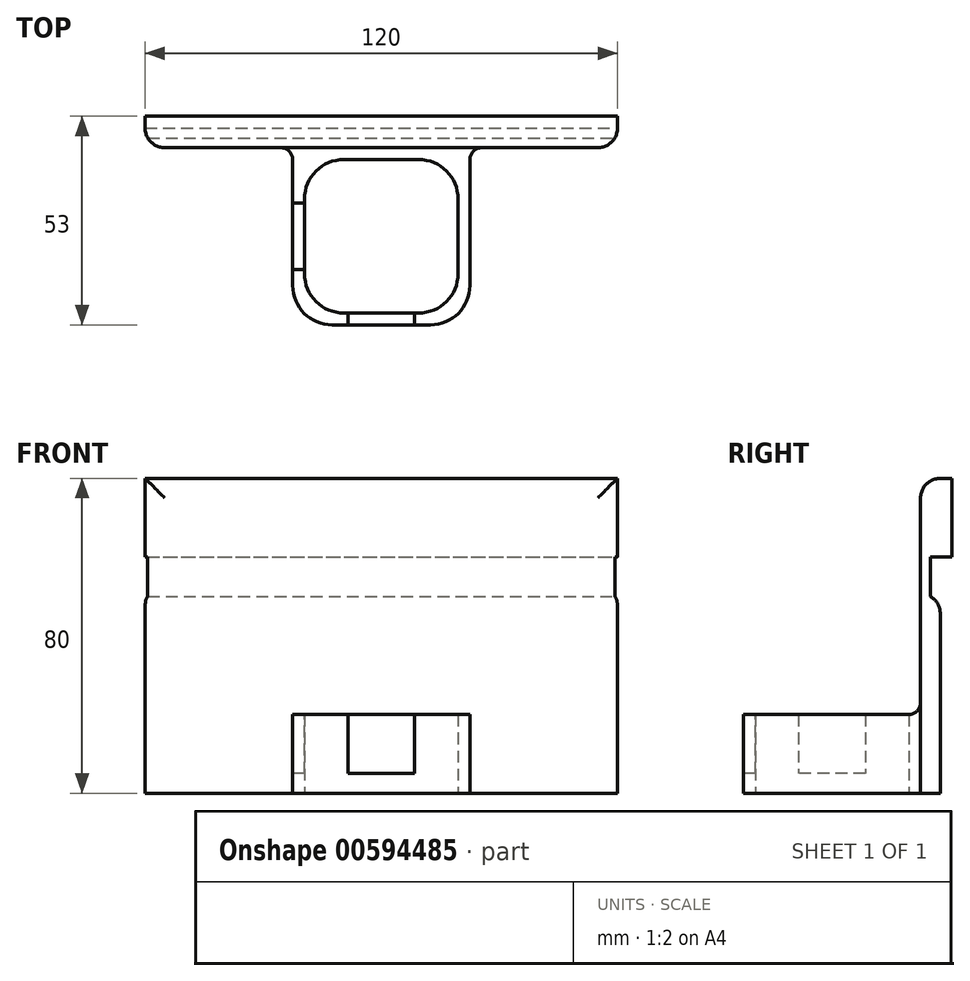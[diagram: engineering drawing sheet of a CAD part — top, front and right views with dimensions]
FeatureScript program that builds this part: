
annotation { "Feature Type Name" : "Feature", "Feature Type Description" : "" }
export const myFeature = defineFeature(function(context is Context, id is Id, definition is map)
    precondition{}
    {
        {
            var Q0;
            Q0=qCreatedBy(makeId("Top.planeOp"),FACE);
            var sketch = newSketch(context, id + "F0", { "sketchPlane" : qUnion([Q0])});
            skLineSegment(sketch, "E0.bottom", {"start": v(-23.05, 24.16) * mm, "end": v(-4.05, 24.16) * mm});
            skLineSegment(sketch, "E0.top", {"start": v(-23.05, -14.84) * mm, "end": v(-4.05, -14.84) * mm});
            skLineSegment(sketch, "E0.left", {"start": v(-33.05, 14.16) * mm, "end": v(-33.05, -4.84) * mm});
            skLineSegment(sketch, "E0.right", {"start": v(5.95, 14.16) * mm, "end": v(5.95, -4.84) * mm});
            skPoint(sketch, "E1.visualSharp", {"position": v(-33.05, 24.16) * mm});
            skArc(sketch, "E1.filletArc", {"start": v(-23.05, 24.16) * mm, "mid": v(-30.12, 21.23) * mm, "end": v(-33.05, 14.16) * mm});
            skPoint(sketch, "E2.visualSharp", {"position": v(5.95, 24.16) * mm});
            skArc(sketch, "E2.filletArc", {"start": v(5.95, 14.16) * mm, "mid": v(3.02, 21.23) * mm, "end": v(-4.05, 24.16) * mm});
            skPoint(sketch, "E3.visualSharp", {"position": v(-33.05, -14.84) * mm});
            skArc(sketch, "E3.filletArc", {"start": v(-33.05, -4.84) * mm, "mid": v(-30.12, -11.9) * mm, "end": v(-23.05, -14.84) * mm});
            skPoint(sketch, "E4.visualSharp", {"position": v(5.95, -14.84) * mm});
            skArc(sketch, "E4.filletArc", {"start": v(-4.05, -14.84) * mm, "mid": v(3.02, -11.9) * mm, "end": v(5.95, -4.84) * mm});
            skLineSegment(sketch, "E5.bottom", {"start": v(-36.05, 27.16) * mm, "end": v(8.95, 27.16) * mm});
            skLineSegment(sketch, "E5.top", {"start": v(-26.05, -17.84) * mm, "end": v(-1.05, -17.84) * mm});
            skLineSegment(sketch, "E5.left", {"start": v(-36.05, 27.16) * mm, "end": v(-36.05, -7.84) * mm});
            skLineSegment(sketch, "E5.right", {"start": v(8.95, 27.16) * mm, "end": v(8.95, -7.84) * mm});
            skPoint(sketch, "E6.visualSharp", {"position": v(-36.05, -17.84) * mm});
            skArc(sketch, "E6.filletArc", {"start": v(-36.05, -7.84) * mm, "mid": v(-33.12, -14.9) * mm, "end": v(-26.05, -17.84) * mm});
            skPoint(sketch, "E7.visualSharp", {"position": v(8.95, -17.84) * mm});
            skArc(sketch, "E7.filletArc", {"start": v(-1.05, -17.84) * mm, "mid": v(6.02, -14.9) * mm, "end": v(8.95, -7.84) * mm});
            skSolve(sketch);
        }
        {
            var Q0;
            Q0 = qSketchRegion(id + "F0", true);
            extrude(context, id + "F1", {"entities" : qUnion([Q0]), "depth" : 20 * mm, "offsetDistance" : 25 * mm});
        }
        {
            var Q0;
            Q0=makeQuery(id+"F1.opExtrude","SWEPT_FACE",FACE,{"disambiguationData":[OSD([sQuery(id+"F0.wireOp",EDGE,"E5.top")])]});
            var sketch = newSketch(context, id + "F2", { "sketchPlane" : qUnion([Q0])});
            skLineSegment(sketch, "E8.bottom", {"start": v(-22.05, 20) * mm, "end": v(-5.05, 20) * mm});
            skLineSegment(sketch, "E8.top", {"start": v(-22.05, 5) * mm, "end": v(-5.05, 5) * mm});
            skLineSegment(sketch, "E8.left", {"start": v(-22.05, 20) * mm, "end": v(-22.05, 5) * mm});
            skLineSegment(sketch, "E8.right", {"start": v(-5.05, 20) * mm, "end": v(-5.05, 5) * mm});
            skSolve(sketch);
        }
        {
            var Q0;
            Q0 = qSketchRegion(id + "F2", true);
            extrude(context, id + "F3", {"entities" : qUnion([Q0]), "operationType" : NewBodyOperationType.REMOVE, "oppositeDirection" : true, "depth" : 5 * mm, "offsetDistance" : 25 * mm});
        }
        {
            var Q0;
            Q0=makeQuery(id+"F1.opExtrude","SWEPT_FACE",FACE,{"disambiguationData":[OSD([sQuery(id+"F0.wireOp",EDGE,"E5.left")])]});
            var sketch = newSketch(context, id + "F4", { "sketchPlane" : qUnion([Q0])});
            skLineSegment(sketch, "E9.bottom", {"start": v(-13.16, 20) * mm, "end": v(3.84, 20) * mm});
            skLineSegment(sketch, "E9.top", {"start": v(-13.16, 5) * mm, "end": v(3.84, 5) * mm});
            skLineSegment(sketch, "E9.left", {"start": v(-13.16, 20) * mm, "end": v(-13.16, 5) * mm});
            skLineSegment(sketch, "E9.right", {"start": v(3.84, 20) * mm, "end": v(3.84, 5) * mm});
            skSolve(sketch);
        }
        {
            var Q0;
            Q0 = qSketchRegion(id + "F4", true);
            extrude(context, id + "F5", {"entities" : qUnion([Q0]), "operationType" : NewBodyOperationType.REMOVE, "oppositeDirection" : true, "depth" : 5 * mm, "offsetDistance" : 25 * mm});
        }
        {
            var Q0;
            Q0=makeQuery(id+"F1.opExtrude","SWEPT_FACE",FACE,{"disambiguationData":[OSD([sQuery(id+"F0.wireOp",EDGE,"E5.bottom")])]});
            var sketch = newSketch(context, id + "F6", { "sketchPlane" : qUnion([Q0])});
            skLineSegment(sketch, "E10.bottom", {"start": v(73.55, 0) * mm, "end": v(-46.45, 0) * mm});
            skLineSegment(sketch, "E10.top", {"start": v(73.55, 80) * mm, "end": v(-46.45, 80) * mm});
            skLineSegment(sketch, "E10.left", {"start": v(73.55, 0) * mm, "end": v(73.55, 80) * mm});
            skLineSegment(sketch, "E10.right", {"start": v(-46.45, 0) * mm, "end": v(-46.45, 80) * mm});
            skSolve(sketch);
        }
        {
            var Q0;
            Q0 = qSketchRegion(id + "F6", true);
            extrude(context, id + "F7", {"entities" : qUnion([Q0]), "operationType" : NewBodyOperationType.ADD, "depth" : 5 * mm, "offsetDistance" : 25 * mm});
        }
        {
            var Q0;
            Q0=makeQuery(id+"F7.boolean.opBoolean","MERGE",FACE,{"derivedFrom":[makeQuery(id+"F1.opExtrude","CAP_FACE",FACE,{"disambiguationData":[OSD([sQuery(id+"F0.wireOp",EDGE,"E0.bottom"),sQuery(id+"F0.wireOp",EDGE,"E0.top"),sQuery(id+"F0.wireOp",EDGE,"E0.left"),sQuery(id+"F0.wireOp",EDGE,"E0.right"),sQuery(id+"F0.wireOp",EDGE,"E1.filletArc"),sQuery(id+"F0.wireOp",EDGE,"E2.filletArc"),sQuery(id+"F0.wireOp",EDGE,"E3.filletArc"),sQuery(id+"F0.wireOp",EDGE,"E4.filletArc"),sQuery(id+"F0.wireOp",EDGE,"E5.bottom"),sQuery(id+"F0.wireOp",EDGE,"E5.top"),sQuery(id+"F0.wireOp",EDGE,"E5.left"),sQuery(id+"F0.wireOp",EDGE,"E5.right"),sQuery(id+"F0.wireOp",EDGE,"E6.filletArc"),sQuery(id+"F0.wireOp",EDGE,"E7.filletArc")])],"isStart":true}),makeQuery(id+"F7.opExtrude","SWEPT_FACE",FACE,{"disambiguationData":[OSD([sQuery(id+"F6.wireOp",EDGE,"E10.bottom")])]})]});
            var sketch = newSketch(context, id + "F8", { "sketchPlane" : qUnion([Q0])});
            skLineSegment(sketch, "E11", {"start": v(46.45, -27.16) * mm, "end": v(11.95, -27.16) * mm});
            skLineSegment(sketch, "E12", {"start": v(8.95, -24.16) * mm, "end": v(8.95, 7.84) * mm});
            skLineSegment(sketch, "E13", {"start": v(-73.55, -27.16) * mm, "end": v(-39.05, -27.16) * mm});
            skLineSegment(sketch, "E14", {"start": v(-36.05, -24.16) * mm, "end": v(-36.05, 7.84) * mm});
            skPoint(sketch, "E15.visualSharp", {"position": v(8.95, -27.16) * mm});
            skArc(sketch, "E15.filletArc", {"start": v(8.95, -24.16) * mm, "mid": v(9.83, -26.28) * mm, "end": v(11.95, -27.16) * mm});
            skPoint(sketch, "E16.visualSharp", {"position": v(-36.05, -27.16) * mm});
            skArc(sketch, "E16.filletArc", {"start": v(-39.05, -27.16) * mm, "mid": v(-36.93, -26.28) * mm, "end": v(-36.05, -24.16) * mm});
            skSolve(sketch);
        }
        {
            var Q0;
            {var subQ0=sQuery(id+"F8.wireOp",EDGE,"E16.filletArc");Q0=makeQuery(id+"F8.imprint","IMPRINT",FACE,{"disambiguationData":[TD([[makeQuery(id+"F8.imprint","IMPRINT",EDGE,{"derivedFrom":subQ0}),-1.0]])]});}
            var Q1;
            {var subQ0=sQuery(id+"F8.wireOp",EDGE,"E15.filletArc");Q1=makeQuery(id+"F8.imprint","IMPRINT",FACE,{"disambiguationData":[TD([[makeQuery(id+"F8.imprint","IMPRINT",EDGE,{"derivedFrom":subQ0}),-1.0]])]});}
            extrude(context, id + "F9", {"entities" : qUnion([Q0, Q1]), "operationType" : NewBodyOperationType.ADD, "oppositeDirection" : true, "depth" : 20 * mm, "offsetDistance" : 25 * mm});
        }
        {
            var Q0;
            Q0=makeQuery(id+"F1.opExtrude","SWEPT_FACE",FACE,{"disambiguationData":[OSD([sQuery(id+"F0.wireOp",EDGE,"E5.right")])]});
            var sketch = newSketch(context, id + "F10", { "sketchPlane" : qUnion([Q0])});
            skLineSegment(sketch, "E17", {"start": v(24.16, 20) * mm, "end": v(24.16, 20) * mm});
            skLineSegment(sketch, "E18", {"start": v(27.16, 23) * mm, "end": v(27.16, 24) * mm});
            skPoint(sketch, "E19.visualSharp", {"position": v(27.16, 20) * mm});
            skArc(sketch, "E19.filletArc", {"start": v(24.16, 20) * mm, "mid": v(26.28, 20.88) * mm, "end": v(27.16, 23) * mm});
            skLineSegment(sketch, "E20", {"start": v(24.16, 20) * mm, "end": v(27.16, 20) * mm});
            skLineSegment(sketch, "E21", {"start": v(27.16, 20) * mm, "end": v(27.16, 23) * mm});
            skSolve(sketch);
        }
        {
            var Q0;
            Q0=makeQuery(id+"F10.imprint","IMPRINT",FACE,{"disambiguationData":[TD([[makeQuery(id+"F10.imprint","IMPRINT",EDGE,{"derivedFrom":sQuery(id+"F10.wireOp",EDGE,"E19.filletArc")}),-1.0]])]});
            extrude(context, id + "F11", {"entities" : qUnion([Q0]), "operationType" : NewBodyOperationType.ADD, "oppositeDirection" : true, "depth" : 45 * mm, "offsetDistance" : 25 * mm});
        }
        {
            var Q0;
            Q0=makeQuery(id+"F11.opExtrude","CAP_FACE",FACE,{"disambiguationData":[OSD([sQuery(id+"F10.wireOp",EDGE,"E19.filletArc"),sQuery(id+"F10.wireOp",EDGE,"E20"),sQuery(id+"F10.wireOp",EDGE,"E21")])],"isStart":true});
            var Q1;
            Q1=makeQuery(id+"F11.opExtrude","CAP_EDGE",EDGE,{"disambiguationData":[OSD([sQuery(id+"F10.wireOp",EDGE,"E20")])],"isStart":true});
            revolve(context, id + "F12", {"operationType" : NewBodyOperationType.ADD, "entities" : qUnion([Q0]), "axis" : qUnion([Q1]), "revolveType" : RevolveType.FULL});
        }
        {
            var Q0;
            Q0=makeQuery(id+"F11.opExtrude","CAP_FACE",FACE,{"disambiguationData":[OSD([sQuery(id+"F10.wireOp",EDGE,"E19.filletArc"),sQuery(id+"F10.wireOp",EDGE,"E20"),sQuery(id+"F10.wireOp",EDGE,"E21")])],"isStart":false});
            var Q1;
            Q1=makeQuery(id+"F11.opExtrude","CAP_EDGE",EDGE,{"disambiguationData":[OSD([sQuery(id+"F10.wireOp",EDGE,"E20")])],"isStart":false});
            revolve(context, id + "F13", {"operationType" : NewBodyOperationType.ADD, "entities" : qUnion([Q0]), "axis" : qUnion([Q1]), "revolveType" : RevolveType.FULL});
        }
        {
            var Q0;
            Q0=makeQuery(id+"F7.opExtrude","CAP_EDGE",EDGE,{"disambiguationData":[OSD([sQuery(id+"F6.wireOp",EDGE,"E10.left")])],"isStart":true});
            var Q1;
            Q1=makeQuery(id+"F7.opExtrude","CAP_EDGE",EDGE,{"disambiguationData":[OSD([sQuery(id+"F6.wireOp",EDGE,"E10.top")])],"isStart":true});
            var Q2;
            Q2=makeQuery(id+"F7.opExtrude","CAP_EDGE",EDGE,{"disambiguationData":[OSD([sQuery(id+"F6.wireOp",EDGE,"E10.right")])],"isStart":true});
            fillet(context, id + "F14", {"entities" : qUnion([Q0, Q1, Q2]), "radius" : 5 * mm, "tangentPropagation" : true, "allowEdgeOverflow" : false});
        }
        {
            var Q0;
            Q0=makeQuery(id+"F7.opExtrude","CAP_FACE",FACE,{"disambiguationData":[OSD([sQuery(id+"F6.wireOp",EDGE,"E10.bottom"),sQuery(id+"F6.wireOp",EDGE,"E10.top"),sQuery(id+"F6.wireOp",EDGE,"E10.left"),sQuery(id+"F6.wireOp",EDGE,"E10.right")])],"isStart":false});
            var sketch = newSketch(context, id + "F15", { "sketchPlane" : qUnion([Q0])});
            skLineSegment(sketch, "E22.bottom", {"start": v(73.55, 50) * mm, "end": v(-46.45, 50) * mm});
            skLineSegment(sketch, "E22.top", {"start": v(73.55, 60) * mm, "end": v(-46.45, 60) * mm});
            skLineSegment(sketch, "E22.left", {"start": v(73.55, 50) * mm, "end": v(73.55, 60) * mm});
            skLineSegment(sketch, "E22.right", {"start": v(-46.45, 50) * mm, "end": v(-46.45, 60) * mm});
            skSolve(sketch);
        }
        {
            var Q0;
            Q0 = qSketchRegion(id + "F15", true);
            extrude(context, id + "F16", {"entities" : qUnion([Q0]), "operationType" : NewBodyOperationType.REMOVE, "oppositeDirection" : true, "depth" : 2.5 * mm, "offsetDistance" : 25 * mm});
        }
        {
            var Q0;
            {var subQ0=sQuery(id+"F6.wireOp",EDGE,"E10.top");var subQ1=sQuery(id+"F6.wireOp",EDGE,"E10.left");var subQ2=sQuery(id+"F6.wireOp",EDGE,"E10.right");Q0=makeQuery(id+"F16.boolean.opBoolean","SPLIT",FACE,{"disambiguationData":[TD([makeQuery(id+"F14.opFillet","BLEND_FACE",FACE,{"disambiguationData":[OSD([subQ0])]})])],"derivedFrom":makeQuery(id+"F7.opExtrude","CAP_FACE",FACE,{"disambiguationData":[OSD([sQuery(id+"F6.wireOp",EDGE,"E10.bottom"),subQ0,subQ1,subQ2])],"isStart":false})});}
            extrude(context, id + "F17", {"entities" : qUnion([Q0]), "operationType" : NewBodyOperationType.ADD, "depth" : 3 * mm, "offsetDistance" : 25 * mm});
        }
        {
            var Q0;
            Q0=makeQuery(id+"F16.boolean.opBoolean","COPY",EDGE,{"derivedFrom":makeQuery(id+"F16.opExtrude","CAP_EDGE",EDGE,{"disambiguationData":[OSD([sQuery(id+"F15.wireOp",EDGE,"E22.bottom")])],"isStart":true})});
            fillet(context, id + "F18", {"entities" : qUnion([Q0]), "radius" : 5 * mm, "tangentPropagation" : true, "allowEdgeOverflow" : false});
        }
    });
